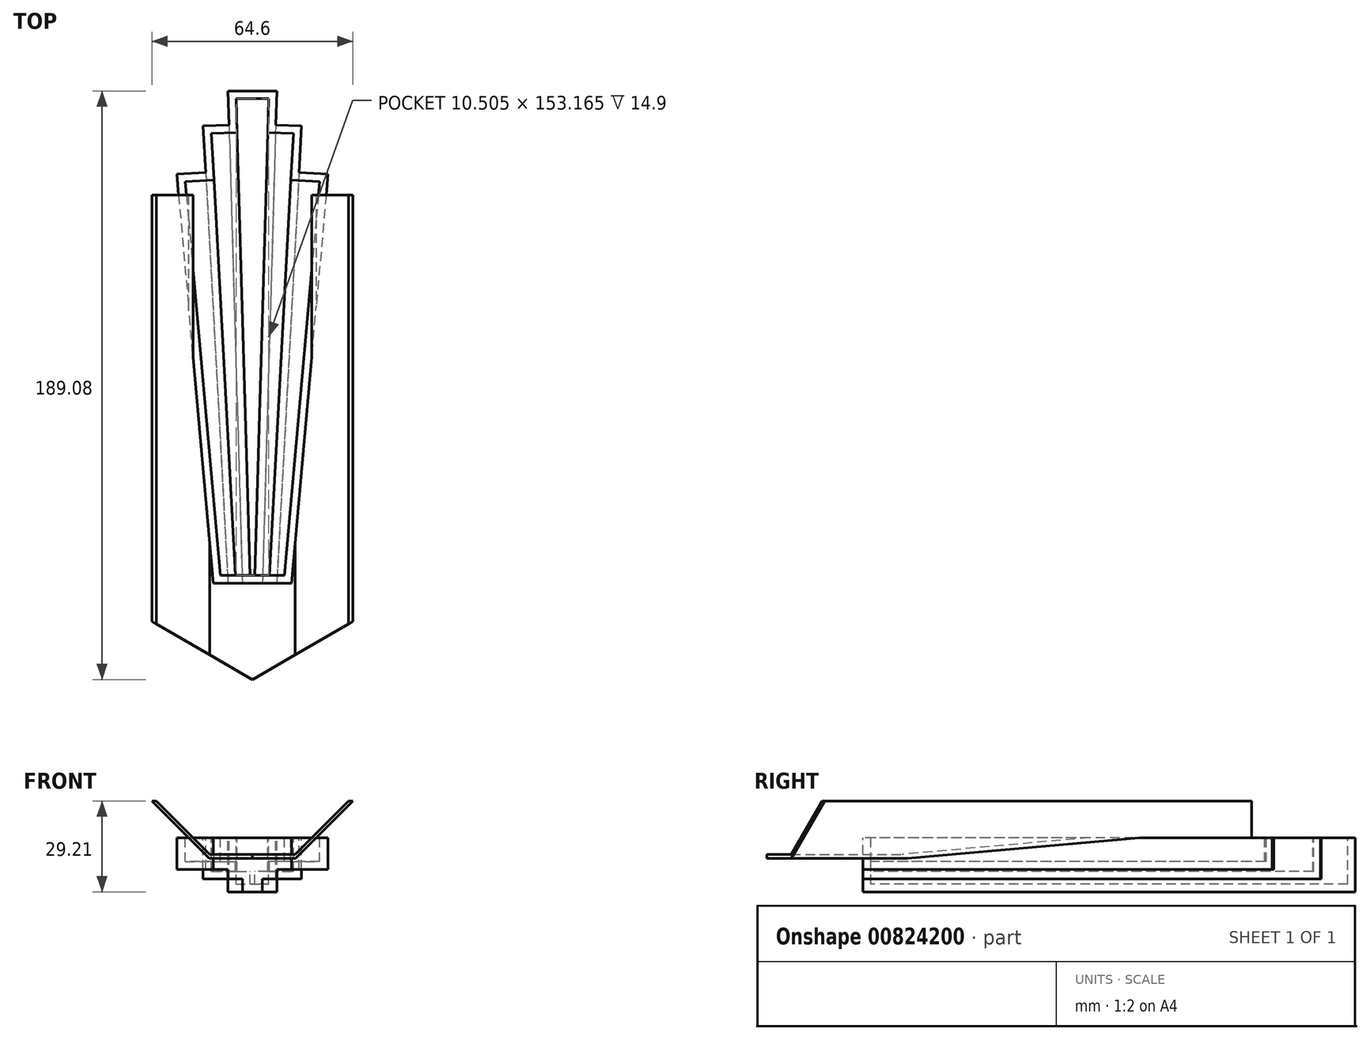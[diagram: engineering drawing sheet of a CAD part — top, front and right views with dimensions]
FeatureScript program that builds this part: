
annotation { "Feature Type Name" : "Feature", "Feature Type Description" : "" }
export const myFeature = defineFeature(function(context is Context, id is Id, definition is map)
    precondition{}
    {
        {
            var Q0;
            Q0=qCreatedBy(makeId("Front.planeOp"),FACE);
            var sketch = newSketch(context, id + "F0", { "sketchPlane" : qUnion([Q0])});
            skLineSegment(sketch, "E0.1", {"start": v(32.3, -14.89) * mm, "end": v(13.82, -33.37) * mm});
            skLineSegment(sketch, "E0.2", {"start": v(13.82, -33.37) * mm, "end": v(-13.82, -33.37) * mm});
            skLineSegment(sketch, "E0.3", {"start": v(-13.82, -33.37) * mm, "end": v(-32.3, -14.89) * mm});
            skLineSegment(sketch, "E1", {"start": v(-30.86, -14.89) * mm, "end": v(-13.67, -32.08) * mm});
            skLineSegment(sketch, "E2", {"start": v(-13.67, -32.08) * mm, "end": v(0, -32.08) * mm});
            skLineSegment(sketch, "E3.MirrorCS", {"start": v(30.86, -14.89) * mm, "end": v(13.67, -32.08) * mm});
            skLineSegment(sketch, "E4.MirrorCS", {"start": v(13.67, -32.08) * mm, "end": v(0, -32.08) * mm});
            skPoint(sketch, "E5.MirrorCS.start.orphan", {"position": v(30.86, -14.89) * mm});
            skLineSegment(sketch, "E6", {"start": v(-30.86, -14.89) * mm, "end": v(-32.3, -14.89) * mm});
            skLineSegment(sketch, "E7", {"start": v(30.86, -14.89) * mm, "end": v(32.3, -14.89) * mm});
            skSolve(sketch);
        }
        {
            var Q0;
            Q0=makeQuery(id+"F0.imprint","IMPRINT",FACE,{"disambiguationData":[TD([[makeQuery(id+"F0.imprint","IMPRINT",EDGE,{"derivedFrom":sQuery(id+"F0.wireOp",EDGE,"E0.1")}),-1.0]])]});
            extrude(context, id + "F1", {"entities" : qUnion([Q0]), "depth" : 45.72 * mm, "offsetDistance" : 25.4 * mm});
        }
        {
            var Q0;
            Q0=makeQuery(id+"F1.opExtrude","SWEPT_FACE",FACE,{"disambiguationData":[OSD([sQuery(id+"F0.wireOp",EDGE,"E0.2")])]});
            var sketch = newSketch(context, id + "F2", { "sketchPlane" : qUnion([Q0])});
            skArc(sketch, "E8.cCircle", {"start": v(-39.58, 0) * mm, "mid": v(0, -39.58) * mm, "end": v(39.58, 0) * mm, "construction": true});
            skLineSegment(sketch, "E8.0", {"start": v(0, 45.7) * mm, "end": v(39.58, 22.86) * mm});
            skLineSegment(sketch, "E8.1", {"start": v(39.58, 0) * mm, "end": v(39.58, -22.85) * mm});
            skLineSegment(sketch, "E8.2", {"start": v(39.58, -22.85) * mm, "end": v(0, -45.7) * mm});
            skLineSegment(sketch, "E8.3", {"start": v(0, -45.7) * mm, "end": v(-39.58, -22.86) * mm});
            skLineSegment(sketch, "E8.4", {"start": v(-39.58, -22.86) * mm, "end": v(-39.58, 0) * mm});
            skLineSegment(sketch, "E8.5", {"start": v(-39.58, 22.85) * mm, "end": v(0, 45.7) * mm});
            skLineSegment(sketch, "E9", {"start": v(-39.58, 22.85) * mm, "end": v(-39.58, 58.4) * mm});
            skLineSegment(sketch, "E10", {"start": v(-39.58, 58.4) * mm, "end": v(39.34, 57.95) * mm});
            skLineSegment(sketch, "E11", {"start": v(39.34, 57.95) * mm, "end": v(39.58, 22.86) * mm});
            skSolve(sketch);
        }
        {
            var Q0;
            {var subQ0=sQuery(id+"F2.wireOp",EDGE,"E9");Q0=makeQuery(id+"F2.imprint","IMPRINT",FACE,{"disambiguationData":[TD([[makeQuery(id+"F2.imprint","IMPRINT",EDGE,{"derivedFrom":subQ0}),-1.0]])]});}
            extrude(context, id + "F3", {"entities" : qUnion([Q0]), "operationType" : NewBodyOperationType.REMOVE, "oppositeDirection" : true, "depth" : 25.4 * mm, "offsetDistance" : 25.4 * mm});
        }
        {
            var Q0;
            {var subQ0=sQuery(id+"F0.wireOp",EDGE,"E0.2");var subQ1=makeQuery(id+"F1.opExtrude","CAP_EDGE",EDGE,{"disambiguationData":[OSD([subQ0])],"isStart":false});Q0=makeQuery(id+"F2.imprint","IMPRINT",FACE,{"disambiguationData":[TD([[makeQuery(id+"F2.imprint","IMPRINT",EDGE,{"derivedFrom":subQ1}),1.0]])]});}
            extrude(context, id + "F4", {"entities" : qUnion([Q0]), "operationType" : NewBodyOperationType.REMOVE, "oppositeDirection" : true, "depth" : 25.4 * mm, "offsetDistance" : 25.4 * mm});
        }
        {
            var Q0;
            Q0=qCreatedBy(makeId("Top.planeOp"),FACE);
            var sketch = newSketch(context, id + "F5", { "sketchPlane" : qUnion([Q0])});
            skLineSegment(sketch, "E12", {"start": v(0, 143.38) * mm, "end": v(-7.83, 143.38) * mm});
            skLineSegment(sketch, "E13", {"start": v(-7.83, 143.38) * mm, "end": v(-3.21, -14.78) * mm});
            skLineSegment(sketch, "E14", {"start": v(0, -14.78) * mm, "end": v(-3.21, -14.78) * mm});
            skLineSegment(sketch, "E15", {"start": v(-7.5, 132.38) * mm, "end": v(-15.8, 132.14) * mm});
            skLineSegment(sketch, "E16", {"start": v(-15.8, 132.14) * mm, "end": v(-7.83, -14.78) * mm});
            skLineSegment(sketch, "E17", {"start": v(-14.99, 117.14) * mm, "end": v(-24.3, 116.63) * mm});
            skLineSegment(sketch, "E18", {"start": v(-24.3, 116.63) * mm, "end": v(-12.55, -14.78) * mm});
            skLineSegment(sketch, "E19", {"start": v(-12.55, -14.78) * mm, "end": v(-3.21, -14.78) * mm});
            skLineSegment(sketch, "E20.MirrorCS", {"start": v(0, 143.38) * mm, "end": v(7.83, 143.38) * mm});
            skLineSegment(sketch, "E21.MirrorCS", {"start": v(7.83, 143.38) * mm, "end": v(3.21, -14.78) * mm});
            skLineSegment(sketch, "E22.MirrorCS", {"start": v(7.5, 132.38) * mm, "end": v(15.8, 132.14) * mm});
            skLineSegment(sketch, "E23.MirrorCS", {"start": v(15.8, 132.14) * mm, "end": v(7.83, -14.78) * mm});
            skLineSegment(sketch, "E24.MirrorCS", {"start": v(14.99, 117.14) * mm, "end": v(24.3, 116.63) * mm});
            skLineSegment(sketch, "E25.MirrorCS", {"start": v(24.3, 116.63) * mm, "end": v(12.55, -14.78) * mm});
            skLineSegment(sketch, "E26.MirrorCS", {"start": v(0, -14.78) * mm, "end": v(3.21, -14.78) * mm});
            skLineSegment(sketch, "E27.MirrorCS", {"start": v(12.55, -14.78) * mm, "end": v(3.21, -14.78) * mm});
            skSolve(sketch);
        }
        {
            var Q0;
            {var subQ6=sQuery(id+"F5.wireOp",EDGE,"E12");Q0=makeQuery(id+"F5.imprint","IMPRINT",FACE,{"disambiguationData":[TD([[makeQuery(id+"F5.imprint","IMPRINT",EDGE,{"derivedFrom":subQ6}),1.0]])]});}
            extrude(context, id + "F6", {"entities" : qUnion([Q0]), "operationType" : NewBodyOperationType.ADD, "oppositeDirection" : true, "depth" : 44.1 * mm, "offsetDistance" : 25 * mm});
        }
        {
            var Q0;
            {var subQ4=sQuery(id+"F5.wireOp",EDGE,"E22.MirrorCS");Q0=makeQuery(id+"F5.imprint","IMPRINT",FACE,{"disambiguationData":[TD([[makeQuery(id+"F5.imprint","IMPRINT",EDGE,{"derivedFrom":subQ4}),-1.0]])]});}
            extrude(context, id + "F7", {"entities" : qUnion([Q0]), "operationType" : NewBodyOperationType.ADD, "oppositeDirection" : true, "depth" : 40 * mm, "offsetDistance" : 25 * mm});
        }
        {
            var Q0;
            {var subQ4=sQuery(id+"F5.wireOp",EDGE,"E15");Q0=makeQuery(id+"F5.imprint","IMPRINT",FACE,{"disambiguationData":[TD([[makeQuery(id+"F5.imprint","IMPRINT",EDGE,{"derivedFrom":subQ4}),1.0]])]});}
            extrude(context, id + "F8", {"entities" : qUnion([Q0]), "operationType" : NewBodyOperationType.ADD, "oppositeDirection" : true, "depth" : 40 * mm, "offsetDistance" : 25 * mm});
        }
        {
            var Q0;
            {var subQ3=sQuery(id+"F5.wireOp",EDGE,"E17");Q0=makeQuery(id+"F5.imprint","IMPRINT",FACE,{"disambiguationData":[TD([[makeQuery(id+"F5.imprint","IMPRINT",EDGE,{"derivedFrom":subQ3}),1.0]])]});}
            extrude(context, id + "F9", {"entities" : qUnion([Q0]), "operationType" : NewBodyOperationType.ADD, "oppositeDirection" : true, "depth" : 36.9 * mm, "offsetDistance" : 25 * mm});
        }
        {
            var Q0;
            {var subQ3=sQuery(id+"F5.wireOp",EDGE,"E24.MirrorCS");Q0=makeQuery(id+"F5.imprint","IMPRINT",FACE,{"disambiguationData":[TD([[makeQuery(id+"F5.imprint","IMPRINT",EDGE,{"derivedFrom":subQ3}),-1.0]])]});}
            extrude(context, id + "F10", {"entities" : qUnion([Q0]), "operationType" : NewBodyOperationType.ADD, "oppositeDirection" : true, "depth" : 36.9 * mm, "offsetDistance" : 25 * mm});
        }
        {
            var Q0;
            {var subQ0=sQuery(id+"F5.wireOp",EDGE,"E27.MirrorCS");var subQ1=sQuery(id+"F5.wireOp",EDGE,"E23.MirrorCS");var subQ2=sQuery(id+"F5.wireOp",EDGE,"E19");var subQ3=sQuery(id+"F5.wireOp",EDGE,"E16");var subQ4=sQuery(id+"F5.wireOp",EDGE,"E13");var subQ5=sQuery(id+"F5.wireOp",EDGE,"E21.MirrorCS");Q0=makeQuery(id+"F10.boolean.opBoolean","MERGE",FACE,{"derivedFrom":[makeQuery(id+"F9.boolean.opBoolean","MERGE",FACE,{"derivedFrom":[makeQuery(id+"F8.boolean.opBoolean","MERGE",FACE,{"derivedFrom":[makeQuery(id+"F7.boolean.opBoolean","MERGE",FACE,{"derivedFrom":[makeQuery(id+"F6.opExtrude","CAP_FACE",FACE,{"disambiguationData":[OSD([sQuery(id+"F5.wireOp",EDGE,"E12"),subQ4,sQuery(id+"F5.wireOp",EDGE,"E14"),sQuery(id+"F5.wireOp",EDGE,"E20.MirrorCS"),subQ5,sQuery(id+"F5.wireOp",EDGE,"E26.MirrorCS")])],"isStart":true}),makeQuery(id+"F7.opExtrude","CAP_FACE",FACE,{"disambiguationData":[OSD([subQ5,sQuery(id+"F5.wireOp",EDGE,"E22.MirrorCS"),subQ1,subQ0])],"isStart":true})]}),makeQuery(id+"F8.opExtrude","CAP_FACE",FACE,{"disambiguationData":[OSD([subQ4,sQuery(id+"F5.wireOp",EDGE,"E15"),subQ3,subQ2])],"isStart":true})]}),makeQuery(id+"F9.opExtrude","CAP_FACE",FACE,{"disambiguationData":[OSD([subQ3,sQuery(id+"F5.wireOp",EDGE,"E17"),sQuery(id+"F5.wireOp",EDGE,"E18"),subQ2])],"isStart":true})]}),makeQuery(id+"F10.opExtrude","CAP_FACE",FACE,{"disambiguationData":[OSD([subQ1,sQuery(id+"F5.wireOp",EDGE,"E24.MirrorCS"),sQuery(id+"F5.wireOp",EDGE,"E25.MirrorCS"),subQ0])],"isStart":true})]});}
            extrude(context, id + "F11", {"entities" : qUnion([Q0]), "operationType" : NewBodyOperationType.REMOVE, "oppositeDirection" : true, "depth" : 26.7 * mm, "offsetDistance" : 25 * mm});
        }
        {
            var Q0;
            {var subQ0=sQuery(id+"F0.wireOp",EDGE,"E3.MirrorCS");var subQ1=sQuery(id+"F0.wireOp",EDGE,"E4.MirrorCS");var subQ2=sQuery(id+"F0.wireOp",EDGE,"E2");var subQ3=sQuery(id+"F0.wireOp",EDGE,"E0.2");var subQ4=sQuery(id+"F0.wireOp",EDGE,"E0.1");var subQ5=sQuery(id+"F0.wireOp",EDGE,"E7");Q0=makeQuery(id+"F6.boolean.opBoolean","SPLIT",FACE,{"disambiguationData":[TD([makeQuery(id+"F1.opExtrude","SWEPT_FACE",FACE,{"disambiguationData":[OSD([subQ4])]})])],"derivedFrom":makeQuery(id+"F1.opExtrude","CAP_FACE",FACE,{"disambiguationData":[OSD([subQ4,subQ3,sQuery(id+"F0.wireOp",EDGE,"E0.3"),sQuery(id+"F0.wireOp",EDGE,"E1"),subQ2,subQ0,subQ1,sQuery(id+"F0.wireOp",EDGE,"E6"),subQ5])],"isStart":true})});}
            extrude(context, id + "F12", {"entities" : qUnion([Q0]), "operationType" : NewBodyOperationType.ADD, "depth" : 110 * mm, "offsetDistance" : 25 * mm});
        }
        {
            var Q0;
            {var subQ0=sQuery(id+"F0.wireOp",EDGE,"E4.MirrorCS");var subQ1=sQuery(id+"F0.wireOp",EDGE,"E2");var subQ2=sQuery(id+"F0.wireOp",EDGE,"E1");var subQ3=sQuery(id+"F0.wireOp",EDGE,"E0.3");var subQ4=sQuery(id+"F0.wireOp",EDGE,"E0.2");var subQ5=sQuery(id+"F0.wireOp",EDGE,"E6");Q0=makeQuery(id+"F6.boolean.opBoolean","SPLIT",FACE,{"disambiguationData":[TD([makeQuery(id+"F1.opExtrude","SWEPT_FACE",FACE,{"disambiguationData":[OSD([subQ3])]})])],"derivedFrom":makeQuery(id+"F1.opExtrude","CAP_FACE",FACE,{"disambiguationData":[OSD([sQuery(id+"F0.wireOp",EDGE,"E0.1"),subQ4,subQ3,subQ2,subQ1,sQuery(id+"F0.wireOp",EDGE,"E3.MirrorCS"),subQ0,subQ5,sQuery(id+"F0.wireOp",EDGE,"E7")])],"isStart":true})});}
            extrude(context, id + "F13", {"entities" : qUnion([Q0]), "operationType" : NewBodyOperationType.ADD, "depth" : 110 * mm, "offsetDistance" : 25 * mm});
        }
        {
            var Q0;
            Q0=makeQuery(id+"F11.boolean.opBoolean","COPY",FACE,{"derivedFrom":makeQuery(id+"F11.opExtrude","CAP_FACE",FACE,{"disambiguationData":[OSD([sQuery(id+"F5.wireOp",EDGE,"E12"),sQuery(id+"F5.wireOp",EDGE,"E13"),sQuery(id+"F5.wireOp",EDGE,"E14"),sQuery(id+"F5.wireOp",EDGE,"E15"),sQuery(id+"F5.wireOp",EDGE,"E16"),sQuery(id+"F5.wireOp",EDGE,"E17"),sQuery(id+"F5.wireOp",EDGE,"E18"),sQuery(id+"F5.wireOp",EDGE,"E19"),sQuery(id+"F5.wireOp",EDGE,"E20.MirrorCS"),sQuery(id+"F5.wireOp",EDGE,"E21.MirrorCS"),sQuery(id+"F5.wireOp",EDGE,"E22.MirrorCS"),sQuery(id+"F5.wireOp",EDGE,"E23.MirrorCS"),sQuery(id+"F5.wireOp",EDGE,"E24.MirrorCS"),sQuery(id+"F5.wireOp",EDGE,"E25.MirrorCS"),sQuery(id+"F5.wireOp",EDGE,"E26.MirrorCS"),sQuery(id+"F5.wireOp",EDGE,"E27.MirrorCS")])],"isStart":false})});
            shell(context, id + "F14", {"entities" : qUnion([Q0]), "thickness" : 2.5 * mm});
        }
    });
